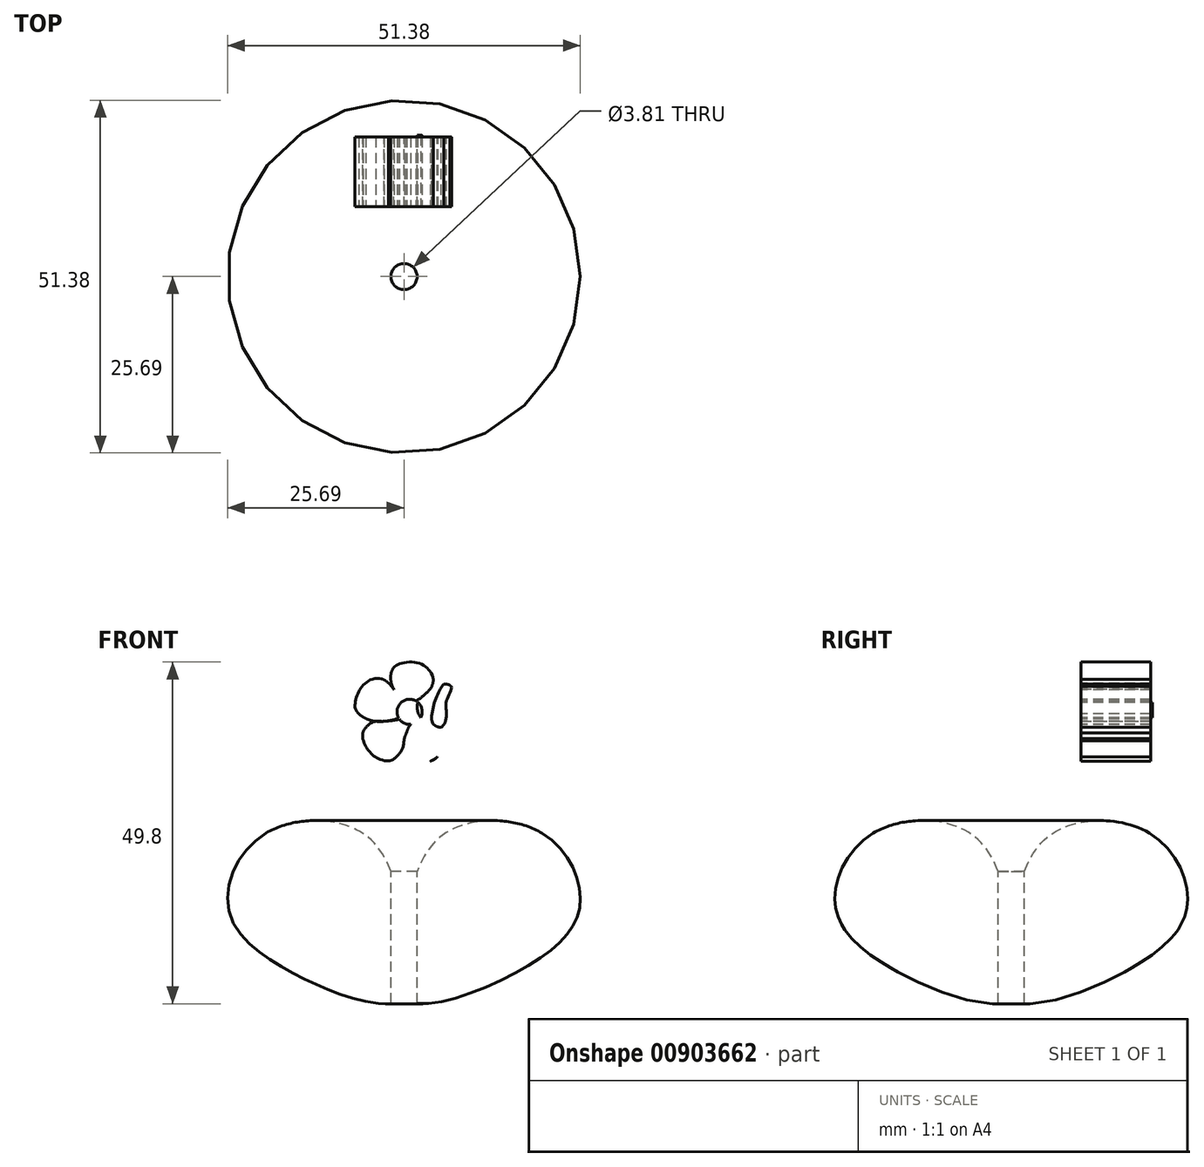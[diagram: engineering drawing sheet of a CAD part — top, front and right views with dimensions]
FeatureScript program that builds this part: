
annotation { "Feature Type Name" : "Feature", "Feature Type Description" : "" }
export const myFeature = defineFeature(function(context is Context, id is Id, definition is map)
    precondition{}
    {
        {
            var Q0;
            Q0=qCreatedBy(makeId("Right.planeOp"),FACE);
            var sketch = newSketch(context, id + "F0", { "sketchPlane" : qUnion([Q0])});
            skFitSpline(sketch, "E0", {"points": [v(0, 0) * mm, v(18.15, 4.9) * mm, v(25.67, 14.06) * mm, v(20.11, 24.2) * mm, v(6.05, 24.2) * mm, v(0, 12.1) * mm, v(0, 0) * mm]});
            skLineSegment(sketch, "E1", {"start": v(20.11, 24.2) * mm, "end": v(17.17, 64.75) * mm});
            skLineSegment(sketch, "E2", {"start": v(17.17, 64.75) * mm, "end": v(0, 63.5) * mm});
            skLineSegment(sketch, "E3", {"start": v(0, 63.5) * mm, "end": v(0, 0) * mm});
            skSolve(sketch);
        }
        {
            var Q0;
            Q0=makeQuery(id+"F0.imprint","IMPRINT",FACE,{"disambiguationData":[TD([[makeQuery(id+"F0.imprint","IMPRINT",EDGE,{"derivedFrom":sQuery(id+"F0.wireOp",EDGE,"E0")}),1.0]])]});
            var Q1;
            Q1=sQuery(id+"F0.wireOp",EDGE,"E3");
            revolve(context, id + "F1", {"surfaceOperationType" : NewSurfaceOperationType.NEW, "entities" : qUnion([Q0]), "axis" : qUnion([Q1]), "revolveType" : RevolveType.FULL});
        }
        {
            var Q0;
            Q0=qCreatedBy(makeId("Front.planeOp"),FACE);
            cPlane(context, id + "F2", {"entities" : qUnion([Q0]), "cplaneType" : CPlaneType.OFFSET, "offset" : 12.7 * mm, "width" : 152.4 * mm, "height" : 152.4 * mm});
        }
        {
            var Q0;
            Q0=qCreatedBy(id+"F2.planeOp",FACE);
            var sketch = newSketch(context, id + "F3", { "sketchPlane" : qUnion([Q0])});
            skText(sketch, "E4", { "text": "G", "fontName": "OpenSans-Regular.ttf"});
            const initialGuessF3  = {"E4": [-0.00984, 0.03098, 1, 0, 0.01864]};
            skSetInitialGuess(sketch, initialGuessF3);
            skSolve(sketch);
        }
        {
            var Q0;
            Q0 = qSketchRegion(id + "F3", true);
            extrude(context, id + "F4", {"entities" : qUnion([Q0]), "operationType" : NewBodyOperationType.REMOVE, "depth" : 7.62 * mm, "offsetDistance" : 25.4 * mm});
        }
        {
            var Q0;
            Q0=qCreatedBy(makeId("Front.planeOp"),FACE);
            cPlane(context, id + "F5", {"entities" : qUnion([Q0]), "cplaneType" : CPlaneType.OFFSET, "offset" : 10.16 * mm, "oppositeDirection" : true, "width" : 152.4 * mm, "height" : 152.4 * mm});
        }
        {
            var Q0;
            Q0=qCreatedBy(id+"F5.planeOp",FACE);
            var sketch = newSketch(context, id + "F6", { "sketchPlane" : qUnion([Q0])});
            skCircle(sketch, "E5", {"center": v(0.82, 41.88) * mm, "radius": 1.83 * mm});
            skArc(sketch, "E6", {"start": v(-1.94, 45.71) * mm, "mid": v(-2.54, 46.28) * mm, "end": v(-3.27, 46.68) * mm});
            skArc(sketch, "E7", {"start": v(-5.98, 38.85) * mm, "mid": v(-5.99, 38.82) * mm, "end": v(-6, 38.79) * mm});
            skArc(sketch, "E8", {"start": v(0.06, 38) * mm, "mid": v(0.02, 37.84) * mm, "end": v(0, 37.67) * mm});
            skFitSpline(sketch, "E9", {"points": [v(4.2, 40.2) * mm, v(6.44, 39.73) * mm, v(7.38, 40.04) * mm, v(8.35, 41.68) * mm, v(8.12, 43.92) * mm, v(6.71, 45.76) * mm, v(5.87, 45.98) * mm, v(4.2, 40.2) * mm]});
            skFitSpline(sketch, "E10", {"points": [v(6.87, 45.6) * mm, v(4.93, 45.76) * mm, v(3.42, 44.64) * mm, v(2.02, 43.27) * mm, v(2.45, 41.03) * mm, v(3.77, 40.35) * mm, v(5.35, 39.63) * mm, v(6.18, 41.23) * mm, v(6.2, 43.53) * mm, v(6.87, 45.6) * mm]});
            skFitSpline(sketch, "E11", {"points": [v(1.7, 43.48) * mm, v(2.57, 44.03) * mm, v(3.96, 45.4) * mm, v(4.29, 46.59) * mm, v(3.7, 47.9) * mm, v(2.5, 48.84) * mm, v(0.63, 49.12) * mm, v(-0.9, 48.74) * mm, v(-1.7, 48.03) * mm, v(-1.94, 46.7) * mm, v(-1.5, 45.23) * mm, v(-0.11, 43.46) * mm, v(1.7, 43.48) * mm]});
            skArc(sketch, "E12.trimOffspring", {"start": v(-1.7, 48.03) * mm, "mid": v(-1.93, 46.6) * mm, "end": v(-1.5, 45.23) * mm});
            skArc(sketch, "E13.trimOffspring", {"start": v(3.96, 45.4) * mm, "mid": v(4.18, 45.98) * mm, "end": v(4.29, 46.59) * mm});
            skFitSpline(sketch, "E14", {"points": [v(-0.42, 43.23) * mm, v(-1.94, 45.71) * mm, v(-3.27, 46.68) * mm, v(-4.96, 46.5) * mm, v(-6.1, 45.56) * mm, v(-6.79, 44.42) * mm, v(-7.11, 43.11) * mm, v(-6.97, 42.08) * mm, v(-5.57, 40.9) * mm, v(-3.25, 40.47) * mm, v(-0.78, 40.99) * mm, v(-0.34, 41.54) * mm, v(-0.42, 43.23) * mm]});
            skArc(sketch, "E15.trimOffspring", {"start": v(-6.97, 42.08) * mm, "mid": v(-6.36, 41.38) * mm, "end": v(-5.57, 40.9) * mm});
            skArc(sketch, "E16.trimOffspring", {"start": v(0.37, 38.82) * mm, "mid": v(0.36, 38.85) * mm, "end": v(0.35, 38.88) * mm});
            skArc(sketch, "E17.trimOffspring", {"start": v(-2.02, 34.76) * mm, "mid": v(-1.94, 34.78) * mm, "end": v(-1.86, 34.8) * mm});
            skFitSpline(sketch, "E18.trimOffspring", {"points": [v(-0.66, 40.8) * mm, v(-2.91, 40.5) * mm, v(-4.08, 40.5) * mm, v(-4.84, 40.23) * mm, v(-5.98, 38.85) * mm, v(-5.7, 37.12) * mm, v(-4.84, 35.84) * mm, v(-3.58, 34.98) * mm, v(-1.86, 34.8) * mm, v(-0.78, 35.68) * mm, v(-0.2, 36.56) * mm, v(0.06, 38) * mm, v(0.28, 38.65) * mm, v(0.57, 40.06) * mm, v(0.36, 40.36) * mm, v(-0.26, 40.84) * mm, v(-0.66, 40.8) * mm]});
            skFitSpline(sketch, "E19", {"points": [v(1, 40.06) * mm, v(0.37, 38.82) * mm, v(0, 37.06) * mm, v(0.1, 35.86) * mm, v(0.96, 34.84) * mm, v(2.1, 34.37) * mm, v(3.82, 34.67) * mm, v(5.66, 36.12) * mm, v(6.08, 37.6) * mm, v(5.09, 39.35) * mm, v(3.28, 40.48) * mm, v(2.23, 40.7) * mm, v(1, 40.06) * mm]});
            skArc(sketch, "E20.trimOffspring", {"start": v(3.82, 34.67) * mm, "mid": v(4.38, 34.93) * mm, "end": v(4.87, 35.3) * mm});
            skSolve(sketch);
        }
        {
            var Q0;
            {var subQ4=sQuery(id+"F6.wireOp",EDGE,"E11");Q0=makeQuery(id+"F6.imprint","IMPRINT",FACE,{"disambiguationData":[TD([[makeQuery(id+"F6.imprint","IMPRINT",EDGE,{"derivedFrom":subQ4}),1.0]])]});}
            var Q1;
            Q1=makeQuery(id+"F6.imprint","IMPRINT",FACE,{"disambiguationData":[TD([[makeQuery(id+"F6.imprint","IMPRINT",EDGE,{"derivedFrom":sQuery(id+"F6.wireOp",EDGE,"E9")}),1.0]])]});
            var Q2;
            {var subQ1=sQuery(id+"F6.wireOp",EDGE,"E19");var subQ5=sQuery(id+"F6.wireOp",EDGE,"E5");var subQ6=makeQuery(id+"F6.imprint","INTERSECT",VERTEX,{"disambiguationData":[OD(0.0)],"derivedFrom":[subQ5,subQ1]});Q2=makeQuery(id+"F6.imprint","IMPRINT",FACE,{"disambiguationData":[TD([[makeQuery(id+"F6.imprint","IMPRINT",EDGE,{"disambiguationData":[TD([[subQ6,-1.0]])],"derivedFrom":subQ5}),-1.0]])]});}
            var Q3;
            {var subQ0=sQuery(id+"F6.wireOp",EDGE,"E14");var subQ1=sQuery(id+"F6.wireOp",EDGE,"E5");var subQ16=makeQuery(id+"F6.imprint","INTERSECT",VERTEX,{"disambiguationData":[OD(0.0)],"derivedFrom":[subQ1,subQ0]});Q3=makeQuery(id+"F6.imprint","IMPRINT",FACE,{"disambiguationData":[TD([[makeQuery(id+"F6.imprint","IMPRINT",EDGE,{"disambiguationData":[TD([[subQ16,-1.0]])],"derivedFrom":subQ1}),-1.0]])]});}
            var Q4;
            {var subQ1=sQuery(id+"F6.wireOp",EDGE,"E5");var subQ6=makeQuery(id+"F6.imprint","INTERSECT",VERTEX,{"derivedFrom":[subQ1,sQuery(id+"F6.wireOp",EDGE,"E10")]});Q4=makeQuery(id+"F6.imprint","IMPRINT",FACE,{"disambiguationData":[TD([[makeQuery(id+"F6.imprint","IMPRINT",EDGE,{"disambiguationData":[TD([[subQ6,-1.0]])],"derivedFrom":subQ1}),1.0]])]});}
            var Q5;
            {var subQ7=sQuery(id+"F6.wireOp",EDGE,"E8");Q5=makeQuery(id+"F6.imprint","IMPRINT",FACE,{"disambiguationData":[TD([[makeQuery(id+"F6.imprint","IMPRINT",EDGE,{"derivedFrom":subQ7}),-1.0]])]});}
            var Q6;
            {var subQ5=sQuery(id+"F6.wireOp",EDGE,"E16.trimOffspring");Q6=makeQuery(id+"F6.imprint","IMPRINT",FACE,{"disambiguationData":[TD([[makeQuery(id+"F6.imprint","IMPRINT",EDGE,{"derivedFrom":subQ5}),-1.0]])]});}
            var Q7;
            {var subQ0=sQuery(id+"F6.wireOp",EDGE,"E11");var subQ1=sQuery(id+"F6.wireOp",EDGE,"E12.trimOffspring");var subQ2=makeQuery(id+"F6.imprint","INTERSECT",VERTEX,{"disambiguationData":[OD(1.0)],"derivedFrom":[subQ1,subQ0]});Q7=makeQuery(id+"F6.imprint","IMPRINT",FACE,{"disambiguationData":[TD([[makeQuery(id+"F6.imprint","IMPRINT",EDGE,{"disambiguationData":[TD([[subQ2,1.0]])],"derivedFrom":subQ1}),1.0]])]});}
            var Q8;
            {var subQ0=sQuery(id+"F6.wireOp",EDGE,"E14");var subQ1=sQuery(id+"F6.wireOp",EDGE,"E11");var subQ2=makeQuery(id+"F6.imprint","INTERSECT",VERTEX,{"disambiguationData":[OD(0.0)],"derivedFrom":[subQ1,subQ0]});Q8=makeQuery(id+"F6.imprint","IMPRINT",FACE,{"disambiguationData":[TD([[makeQuery(id+"F6.imprint","IMPRINT",EDGE,{"disambiguationData":[TD([[subQ2,-1.0]])],"derivedFrom":subQ1}),1.0]])]});}
            var Q9;
            {var subQ0=sQuery(id+"F6.wireOp",EDGE,"E15.trimOffspring");var subQ1=sQuery(id+"F6.wireOp",EDGE,"E14");var subQ2=makeQuery(id+"F6.imprint","INTERSECT",VERTEX,{"disambiguationData":[OD(0.0)],"derivedFrom":[subQ1,subQ0]});Q9=makeQuery(id+"F6.imprint","IMPRINT",FACE,{"disambiguationData":[TD([[makeQuery(id+"F6.imprint","IMPRINT",EDGE,{"disambiguationData":[TD([[subQ2,-1.0]])],"derivedFrom":subQ1}),1.0]])]});}
            var Q10;
            {var subQ0=sQuery(id+"F6.wireOp",EDGE,"E20.trimOffspring");Q10=makeQuery(id+"F6.imprint","IMPRINT",FACE,{"disambiguationData":[TD([[makeQuery(id+"F6.imprint","IMPRINT",EDGE,{"derivedFrom":subQ0}),1.0]])]});}
            var Q11;
            {var subQ0=sQuery(id+"F6.wireOp",EDGE,"E14");var subQ1=sQuery(id+"F6.wireOp",EDGE,"E6");var subQ2=makeQuery(id+"F6.imprint","INTERSECT",VERTEX,{"disambiguationData":[OD(1.0)],"derivedFrom":[subQ1,subQ0]});Q11=makeQuery(id+"F6.imprint","IMPRINT",FACE,{"disambiguationData":[TD([[makeQuery(id+"F6.imprint","IMPRINT",EDGE,{"disambiguationData":[TD([[subQ2,1.0]])],"derivedFrom":subQ1}),-1.0]])]});}
            var Q12;
            {var subQ0=sQuery(id+"F6.wireOp",EDGE,"E14");var subQ1=sQuery(id+"F6.wireOp",EDGE,"E6");var subQ2=makeQuery(id+"F6.imprint","INTERSECT",VERTEX,{"disambiguationData":[OD(0.0)],"derivedFrom":[subQ1,subQ0]});Q12=makeQuery(id+"F6.imprint","IMPRINT",FACE,{"disambiguationData":[TD([[makeQuery(id+"F6.imprint","IMPRINT",EDGE,{"disambiguationData":[TD([[subQ2,-1.0]])],"derivedFrom":subQ1}),1.0]])]});}
            var Q13;
            {var subQ0=sQuery(id+"F6.wireOp",EDGE,"E18.trimOffspring");var subQ1=sQuery(id+"F6.wireOp",EDGE,"E14");var subQ2=makeQuery(id+"F6.imprint","INTERSECT",VERTEX,{"disambiguationData":[OD(0.0)],"derivedFrom":[subQ1,subQ0]});Q13=makeQuery(id+"F6.imprint","IMPRINT",FACE,{"disambiguationData":[TD([[makeQuery(id+"F6.imprint","IMPRINT",EDGE,{"disambiguationData":[TD([[subQ2,1.0]])],"derivedFrom":subQ1}),1.0]])]});}
            var Q14;
            {var subQ0=sQuery(id+"F6.wireOp",EDGE,"E11");var subQ1=sQuery(id+"F6.wireOp",EDGE,"E5");var subQ2=makeQuery(id+"F6.imprint","INTERSECT",VERTEX,{"derivedFrom":[subQ1,subQ0]});Q14=makeQuery(id+"F6.imprint","IMPRINT",FACE,{"disambiguationData":[TD([[makeQuery(id+"F6.imprint","IMPRINT",EDGE,{"disambiguationData":[TD([[subQ2,-1.0]])],"derivedFrom":subQ1}),-1.0]])]});}
            var Q15;
            {var subQ0=sQuery(id+"F6.wireOp",EDGE,"E15.trimOffspring");var subQ1=sQuery(id+"F6.wireOp",EDGE,"E14");var subQ2=makeQuery(id+"F6.imprint","INTERSECT",VERTEX,{"disambiguationData":[OD(1.0)],"derivedFrom":[subQ1,subQ0]});Q15=makeQuery(id+"F6.imprint","IMPRINT",FACE,{"disambiguationData":[TD([[makeQuery(id+"F6.imprint","IMPRINT",EDGE,{"disambiguationData":[TD([[subQ2,1.0]])],"derivedFrom":subQ1}),-1.0]])]});}
            var Q16;
            {var subQ0=sQuery(id+"F6.wireOp",EDGE,"E11");var subQ1=sQuery(id+"F6.wireOp",EDGE,"E12.trimOffspring");var subQ2=makeQuery(id+"F6.imprint","INTERSECT",VERTEX,{"disambiguationData":[OD(0.0)],"derivedFrom":[subQ1,subQ0]});Q16=makeQuery(id+"F6.imprint","IMPRINT",FACE,{"disambiguationData":[TD([[makeQuery(id+"F6.imprint","IMPRINT",EDGE,{"disambiguationData":[TD([[subQ2,-1.0]])],"derivedFrom":subQ1}),-1.0]])]});}
            var Q17;
            {var subQ0=sQuery(id+"F6.wireOp",EDGE,"E17.trimOffspring");Q17=makeQuery(id+"F6.imprint","IMPRINT",FACE,{"disambiguationData":[TD([[makeQuery(id+"F6.imprint","IMPRINT",EDGE,{"derivedFrom":subQ0}),-1.0]])]});}
            var Q18;
            {var subQ0=sQuery(id+"F6.wireOp",EDGE,"E8");Q18=makeQuery(id+"F6.imprint","IMPRINT",FACE,{"disambiguationData":[TD([[makeQuery(id+"F6.imprint","IMPRINT",EDGE,{"derivedFrom":subQ0}),1.0]])]});}
            extrude(context, id + "F7", {"entities" : qUnion([Q0, Q1, Q2, Q3, Q4, Q5, Q6, Q7, Q8, Q9, Q10, Q11, Q12, Q13, Q14, Q15, Q16, Q17, Q18]), "oppositeDirection" : true, "depth" : 10.16 * mm, "offsetDistance" : 25.4 * mm});
        }
        {
            var Q0;
            {var subQ1=sQuery(id+"F6.wireOp",EDGE,"E5");var subQ6=makeQuery(id+"F6.imprint","INTERSECT",VERTEX,{"derivedFrom":[subQ1,sQuery(id+"F6.wireOp",EDGE,"E10")]});Q0=makeQuery(id+"F6.imprint","IMPRINT",FACE,{"disambiguationData":[TD([[makeQuery(id+"F6.imprint","IMPRINT",EDGE,{"disambiguationData":[TD([[subQ6,-1.0]])],"derivedFrom":subQ1}),1.0]])]});}
            extrude(context, id + "F8", {"entities" : qUnion([Q0]), "operationType" : NewBodyOperationType.ADD, "oppositeDirection" : true, "depth" : 10.4 * mm, "offsetDistance" : 25.4 * mm});
        }
        {
            var Q0;
            Q0=qCreatedBy(makeId("Top.planeOp"),FACE);
            cPlane(context, id + "F9", {"entities" : qUnion([Q0]), "cplaneType" : CPlaneType.OFFSET, "offset" : 66.04 * mm, "width" : 152.4 * mm, "height" : 152.4 * mm});
        }
        {
            var Q0;
            Q0=qCreatedBy(id+"F9.planeOp",FACE);
            var sketch = newSketch(context, id + "F10", { "sketchPlane" : qUnion([Q0])});
            skCircle(sketch, "E21", {"center": v(0, 0) * mm, "radius": 1.9 * mm});
            skSolve(sketch);
        }
        {
            var Q0;
            Q0=makeQuery(id+"F10.imprint","IMPRINT",FACE,{"disambiguationData":[TD([[makeQuery(id+"F10.imprint","IMPRINT",EDGE,{"derivedFrom":sQuery(id+"F10.wireOp",EDGE,"E21")}),1.0]])]});
            extrude(context, id + "F11", {"entities" : qUnion([Q0]), "operationType" : NewBodyOperationType.REMOVE, "oppositeDirection" : true, "depth" : 76.2 * mm, "offsetDistance" : 25.4 * mm});
        }
    });
